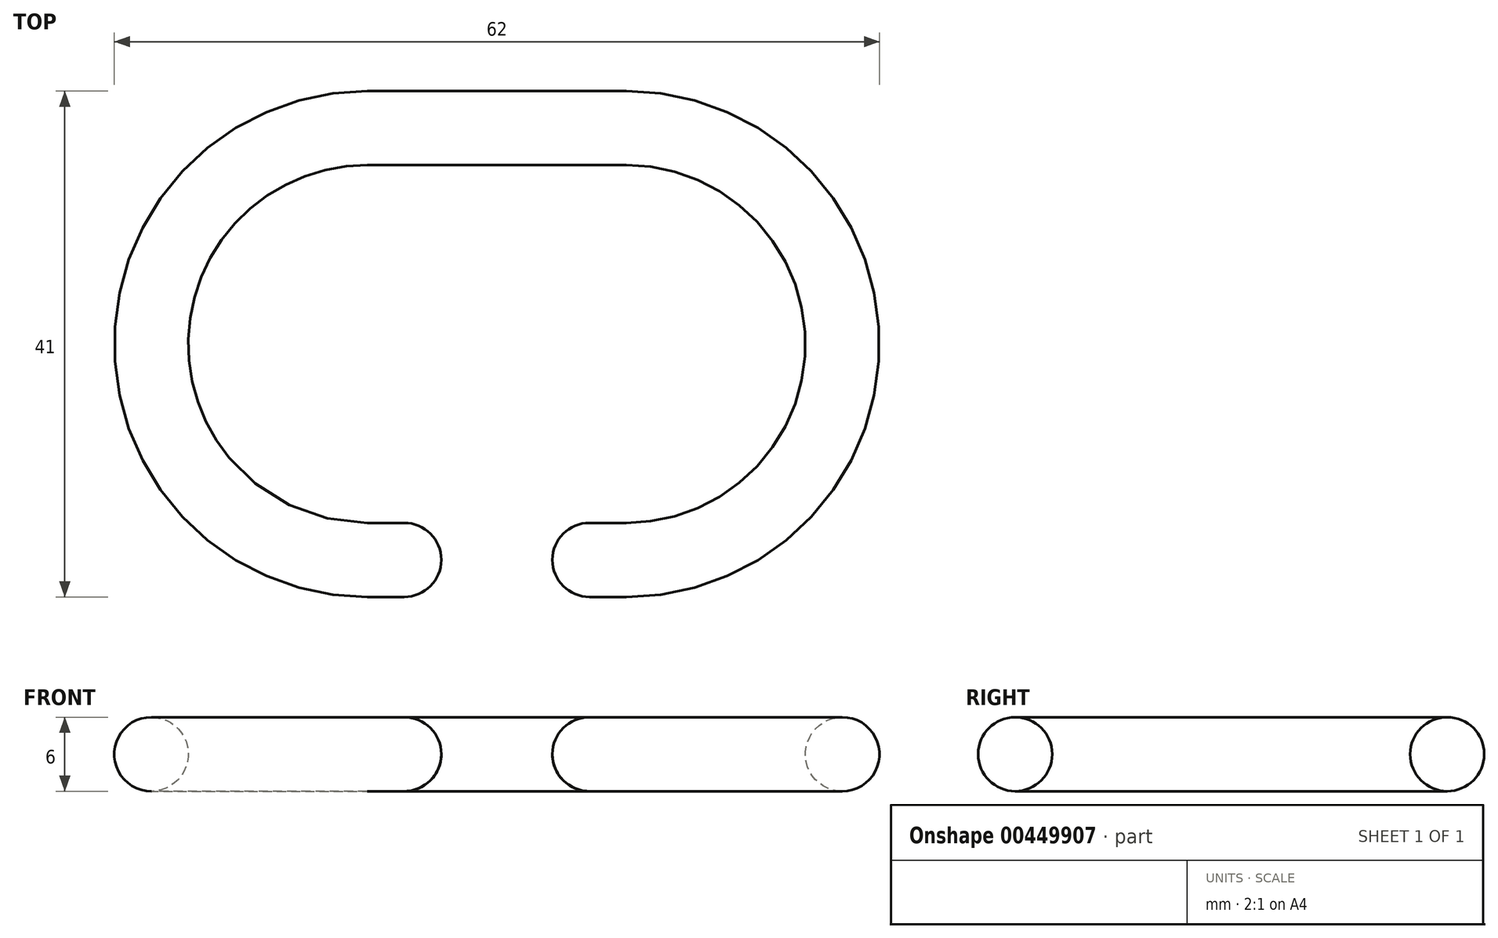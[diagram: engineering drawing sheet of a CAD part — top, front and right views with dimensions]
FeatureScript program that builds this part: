
annotation { "Feature Type Name" : "Feature", "Feature Type Description" : "" }
export const myFeature = defineFeature(function(context is Context, id is Id, definition is map)
    precondition{}
    {
        {
            var Q0;
            Q0=qCreatedBy(makeId("Top.planeOp"),FACE);
            var sketch = newSketch(context, id + "F0", { "sketchPlane" : qUnion([Q0])});
            skLineSegment(sketch, "E0", {"start": v(0, 0) * mm, "end": v(10.5, 0) * mm, "construction": true});
            skLineSegment(sketch, "E1", {"start": v(10.5, 0) * mm, "end": v(28, 0) * mm, "construction": true});
            skLineSegment(sketch, "E2", {"start": v(10.5, 0) * mm, "end": v(10.5, -17.5) * mm, "construction": true});
            skLineSegment(sketch, "E3", {"start": v(10.5, 0) * mm, "end": v(10.5, 17.5) * mm, "construction": true});
            skArc(sketch, "E4", {"start": v(10.5, -17.5) * mm, "mid": v(28, 0) * mm, "end": v(10.5, 17.5) * mm});
            skLineSegment(sketch, "E5", {"start": v(10.5, 17.5) * mm, "end": v(0, 17.5) * mm});
            skLineSegment(sketch, "E6", {"start": v(10.5, -17.5) * mm, "end": v(4.5, -17.5) * mm});
            skLineSegment(sketch, "E7.MirrorCS", {"start": v(-10.5, 17.5) * mm, "end": v(0, 17.5) * mm});
            skArc(sketch, "E8.MirrorCS", {"start": v(-10.5, -17.5) * mm, "mid": v(-28, 0) * mm, "end": v(-10.5, 17.5) * mm});
            skLineSegment(sketch, "E9.MirrorCS", {"start": v(-10.5, -17.5) * mm, "end": v(-4.5, -17.5) * mm});
            skSolve(sketch);
        }
        {
            var Q0;
            Q0=sQuery(id+"F0.wireOp",VERTEX,"E9.MirrorCS.end");
            var Q1;
            Q1=qCreatedBy(makeId("Right.planeOp"),FACE);
            cPlane(context, id + "F1", {"entities" : qUnion([Q0, Q1]), "cplaneType" : CPlaneType.PLANE_POINT, "offset" : 25 * mm, "width" : 150 * mm, "height" : 150 * mm});
        }
        {
            var Q0;
            Q0=qCreatedBy(id+"F1.planeOp",FACE);
            var sketch = newSketch(context, id + "F2", { "sketchPlane" : qUnion([Q0])});
            skCircle(sketch, "E10", {"center": v(-17.5, 0) * mm, "radius": 3 * mm});
            skSolve(sketch);
        }
        {
            var Q0;
            Q0=makeQuery(id+"F2.imprint","IMPRINT",FACE,{"disambiguationData":[TD([[makeQuery(id+"F2.imprint","IMPRINT",EDGE,{"derivedFrom":sQuery(id+"F2.wireOp",EDGE,"E10")}),1.0]])]});
            var Q1;
            Q1=sQuery(id+"F0.wireOp",EDGE,"E9.MirrorCS");
            var Q2;
            Q2=sQuery(id+"F0.wireOp",EDGE,"E8.MirrorCS");
            var Q3;
            Q3=sQuery(id+"F0.wireOp",EDGE,"E7.MirrorCS");
            var Q4;
            Q4=sQuery(id+"F0.wireOp",EDGE,"E5");
            var Q5;
            Q5=sQuery(id+"F0.wireOp",EDGE,"E4");
            var Q6;
            Q6=sQuery(id+"F0.wireOp",EDGE,"E6");
            sweep(context, id + "F3", {"profiles" : qUnion([Q0]), "path" : qUnion([Q1, Q2, Q3, Q4, Q5, Q6])});
        }
        {
            var Q0;
            Q0=makeQuery(id+"F3.opSweep","CAP_EDGE",EDGE,{"disambiguationData":[OSD([sQuery(id+"F0.wireOp",VERTEX,"E9.MirrorCS.end"),sQuery(id+"F2.wireOp",EDGE,"E10")])],"isStart":true});
            var Q1;
            Q1=makeQuery(id+"F3.opSweep","CAP_EDGE",EDGE,{"disambiguationData":[OSD([sQuery(id+"F0.wireOp",VERTEX,"E6.end"),sQuery(id+"F2.wireOp",EDGE,"E10")])],"isStart":false});
            fillet(context, id + "F4", {"entities" : qUnion([Q0, Q1]), "radius" : 3 * mm, "tangentPropagation" : true, "allowEdgeOverflow" : false});
        }
    });
